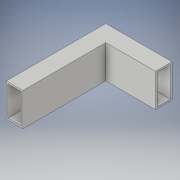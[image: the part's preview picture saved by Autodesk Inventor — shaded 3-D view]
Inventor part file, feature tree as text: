
AUTODESK INVENTOR PART (.ipt)
format: ipt  version: 2018 (Build 220112000, 112)  size: 131,072 bytes
history: native  units: in
note: dims shown in document units (in); Inventor stores cm internally (conversion verified against a paired STEP export)
features: extrude x3, sketch x3
ambient origin geometry x8: Origin, YZ Plane, XZ Plane, XY Plane, X Axis, Y Axis, Z Axis, Center Point
bodies: Body1 (feature_tree)
feature tree (6):
  extrude  "Extrusion12"  Depth=2.0in
  extrude  "Extrusion14"  Depth=0.1in
  extrude  "Extrusion16"  Depth=0.1in
  sketch  "Sketch15"  dims[d46=1.0in d47=2.0in]
  sketch  "Sketch17"  dims[d48=0.1in d49=0.1in]
  sketch  "Sketch20"  dims[d50=0.1in d51=0.1in d52=3.0in d53=0.0in d62=0.1in d63=0.0in d71=1.0in d72=2.0in d73=0.1in d74=0.1in d75=0.1in d76=0.1in d77=0.1in d78=0.0in d79=6.0in d80=0.0in]
